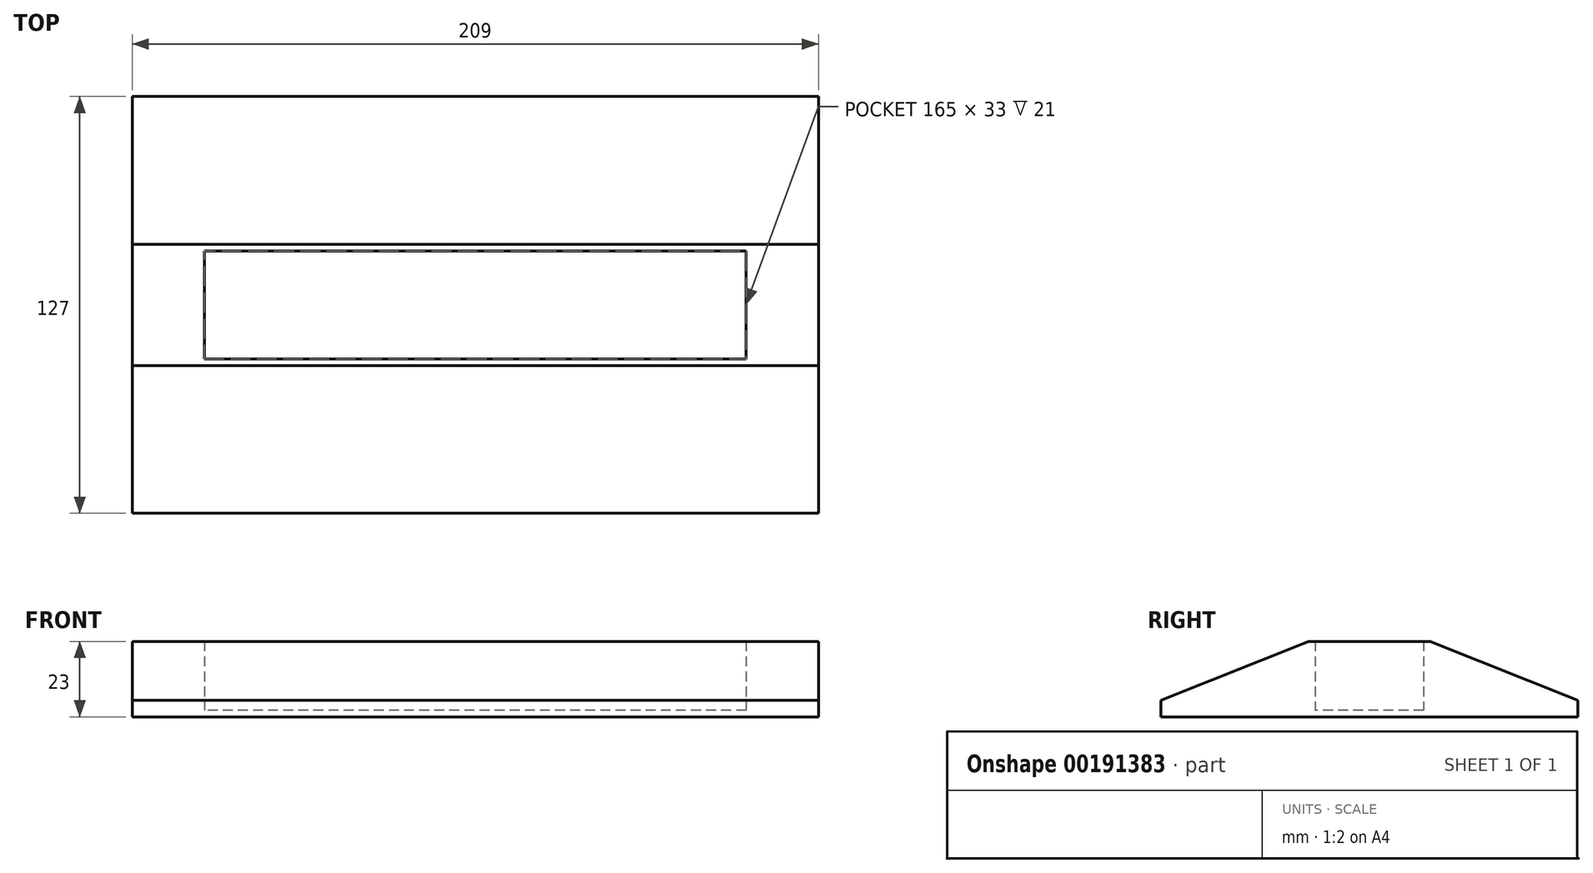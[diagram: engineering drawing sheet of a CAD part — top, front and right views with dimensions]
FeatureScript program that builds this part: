
annotation { "Feature Type Name" : "Feature", "Feature Type Description" : "" }
export const myFeature = defineFeature(function(context is Context, id is Id, definition is map)
    precondition{}
    {
        {
            var Q0;
            Q0=qCreatedBy(makeId("Top.planeOp"),FACE);
            var sketch = newSketch(context, id + "F0", { "sketchPlane" : qUnion([Q0])});
            skLineSegment(sketch, "E0.bottom", {"start": v(82.5, 16.5) * mm, "end": v(-82.5, 16.5) * mm});
            skLineSegment(sketch, "E0.top", {"start": v(82.5, -16.5) * mm, "end": v(-82.5, -16.5) * mm});
            skLineSegment(sketch, "E0.left", {"start": v(82.5, 16.5) * mm, "end": v(82.5, -16.5) * mm});
            skLineSegment(sketch, "E0.right", {"start": v(-82.5, 16.5) * mm, "end": v(-82.5, -16.5) * mm});
            skPoint(sketch, "E0.middle", {"position": v(0, 0) * mm});
            skLineSegment(sketch, "E1.0", {"start": v(84.5, 18.5) * mm, "end": v(-84.5, 18.5) * mm});
            skLineSegment(sketch, "E1.1", {"start": v(84.5, 18.5) * mm, "end": v(84.5, -18.5) * mm});
            skLineSegment(sketch, "E1.2", {"start": v(84.5, -18.5) * mm, "end": v(-84.5, -18.5) * mm});
            skLineSegment(sketch, "E1.3", {"start": v(-84.5, 18.5) * mm, "end": v(-84.5, -18.5) * mm});
            skLineSegment(sketch, "E2.bottom", {"start": v(-84.5, -18.5) * mm, "end": v(-104.5, -18.5) * mm});
            skLineSegment(sketch, "E2.top", {"start": v(-84.5, 18.5) * mm, "end": v(-104.5, 18.5) * mm});
            skLineSegment(sketch, "E2.left", {"start": v(-84.5, -18.5) * mm, "end": v(-84.5, 18.5) * mm});
            skLineSegment(sketch, "E2.right", {"start": v(-104.5, -18.5) * mm, "end": v(-104.5, 18.5) * mm});
            skLineSegment(sketch, "E3.bottom", {"start": v(84.5, -18.5) * mm, "end": v(104.5, -18.5) * mm});
            skLineSegment(sketch, "E3.top", {"start": v(84.5, 18.5) * mm, "end": v(104.5, 18.5) * mm});
            skLineSegment(sketch, "E3.left", {"start": v(84.5, -18.5) * mm, "end": v(84.5, 18.5) * mm});
            skLineSegment(sketch, "E3.right", {"start": v(104.5, -18.5) * mm, "end": v(104.5, 18.5) * mm});
            skSolve(sketch);
        }
        {
            var Q0;
            Q0=makeQuery(id+"F0.imprint","IMPRINT",FACE,{"disambiguationData":[TD([[makeQuery(id+"F0.imprint","IMPRINT",EDGE,{"derivedFrom":sQuery(id+"F0.wireOp",EDGE,"E0.bottom")}),1.0]])]});
            extrude(context, id + "F1", {"entities" : qUnion([Q0]), "depth" : 2 * mm});
        }
        {
            var Q0;
            Q0=makeQuery(id+"F0.imprint","IMPRINT",FACE,{"disambiguationData":[TD([[makeQuery(id+"F0.imprint","IMPRINT",EDGE,{"derivedFrom":sQuery(id+"F0.wireOp",EDGE,"E0.bottom")}),-1.0]])]});
            extrude(context, id + "F2", {"entities" : qUnion([Q0]), "operationType" : NewBodyOperationType.ADD, "depth" : 23 * mm});
        }
        {
            var Q0;
            Q0=makeQuery(id+"F0.imprint","IMPRINT",FACE,{"disambiguationData":[TD([[makeQuery(id+"F0.imprint","IMPRINT",EDGE,{"derivedFrom":sQuery(id+"F0.wireOp",EDGE,"E2.bottom")}),-1.0]])]});
            var Q1;
            Q1=makeQuery(id+"F0.imprint","IMPRINT",FACE,{"disambiguationData":[TD([[makeQuery(id+"F0.imprint","IMPRINT",EDGE,{"derivedFrom":sQuery(id+"F0.wireOp",EDGE,"E3.bottom")}),1.0]])]});
            extrude(context, id + "F3", {"entities" : qUnion([Q0, Q1]), "operationType" : NewBodyOperationType.ADD, "depth" : 23 * mm});
        }
        {
            var Q0;
            Q0=makeQuery(id+"F3.opExtrude","SWEPT_FACE",FACE,{"disambiguationData":[OSD([sQuery(id+"F0.wireOp",EDGE,"E3.right")])]});
            var sketch = newSketch(context, id + "F4", { "sketchPlane" : qUnion([Q0])});
            skLineSegment(sketch, "E4", {"start": v(-18.5, 0) * mm, "end": v(-63.5, 0) * mm});
            skLineSegment(sketch, "E5", {"start": v(-63.5, 0) * mm, "end": v(-63.5, 5) * mm});
            skLineSegment(sketch, "E6", {"start": v(-63.5, 5) * mm, "end": v(-18.5, 23) * mm});
            skLineSegment(sketch, "E7", {"start": v(18.5, 0) * mm, "end": v(63.5, 0) * mm});
            skLineSegment(sketch, "E8", {"start": v(63.5, 0) * mm, "end": v(63.5, 5) * mm});
            skLineSegment(sketch, "E9", {"start": v(63.5, 5) * mm, "end": v(18.5, 23) * mm});
            skSolve(sketch);
        }
        {
            var Q0;
            Q0=makeQuery(id+"F4.imprint","IMPRINT",FACE,{"disambiguationData":[TD([[makeQuery(id+"F4.imprint","IMPRINT",EDGE,{"derivedFrom":sQuery(id+"F4.wireOp",EDGE,"E4")}),-1.0]])]});
            var Q1;
            Q1=makeQuery(id+"F4.imprint","IMPRINT",FACE,{"disambiguationData":[TD([[makeQuery(id+"F4.imprint","IMPRINT",EDGE,{"derivedFrom":sQuery(id+"F4.wireOp",EDGE,"E7")}),1.0]])]});
            extrude(context, id + "F5", {"entities" : qUnion([Q0, Q1]), "operationType" : NewBodyOperationType.ADD, "oppositeDirection" : true, "depth" : 209 * mm});
        }
    });
